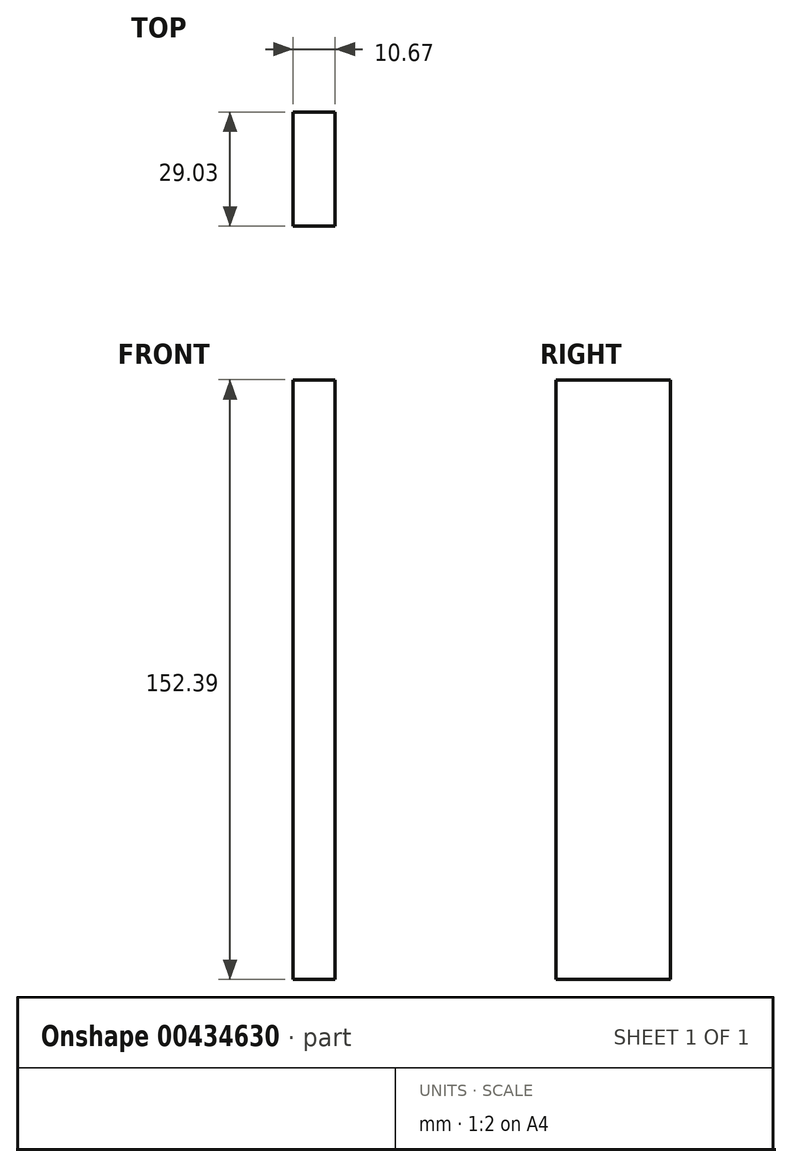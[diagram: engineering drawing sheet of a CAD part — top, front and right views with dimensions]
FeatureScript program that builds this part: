
annotation { "Feature Type Name" : "Feature", "Feature Type Description" : "" }
export const myFeature = defineFeature(function(context is Context, id is Id, definition is map)
    precondition{}
    {
        {
            var Q0;
            Q0=qCreatedBy(makeId("Right.planeOp"),FACE);
            var sketch = newSketch(context, id + "F0", { "sketchPlane" : qUnion([Q0])});
            skLineSegment(sketch, "E0.bottom", {"start": v(-76.05, 75.76) * mm, "end": v(-47.02, 75.76) * mm});
            skLineSegment(sketch, "E0.top", {"start": v(-76.05, -76.63) * mm, "end": v(-47.02, -76.63) * mm});
            skLineSegment(sketch, "E0.left", {"start": v(-76.05, 75.76) * mm, "end": v(-76.05, -76.63) * mm});
            skLineSegment(sketch, "E0.right", {"start": v(-47.02, 75.76) * mm, "end": v(-47.02, -76.63) * mm});
            skSolve(sketch);
        }
        {
            var Q0;
            Q0=makeQuery(id+"F0.imprint","IMPRINT",FACE,{"disambiguationData":[TD([[makeQuery(id+"F0.imprint","IMPRINT",EDGE,{"derivedFrom":sQuery(id+"F0.wireOp",EDGE,"E0.bottom")}),-1.0]])]});
            extrude(context, id + "F1", {"entities" : qUnion([Q0]), "depth" : 10.67 * mm});
        }
    });
